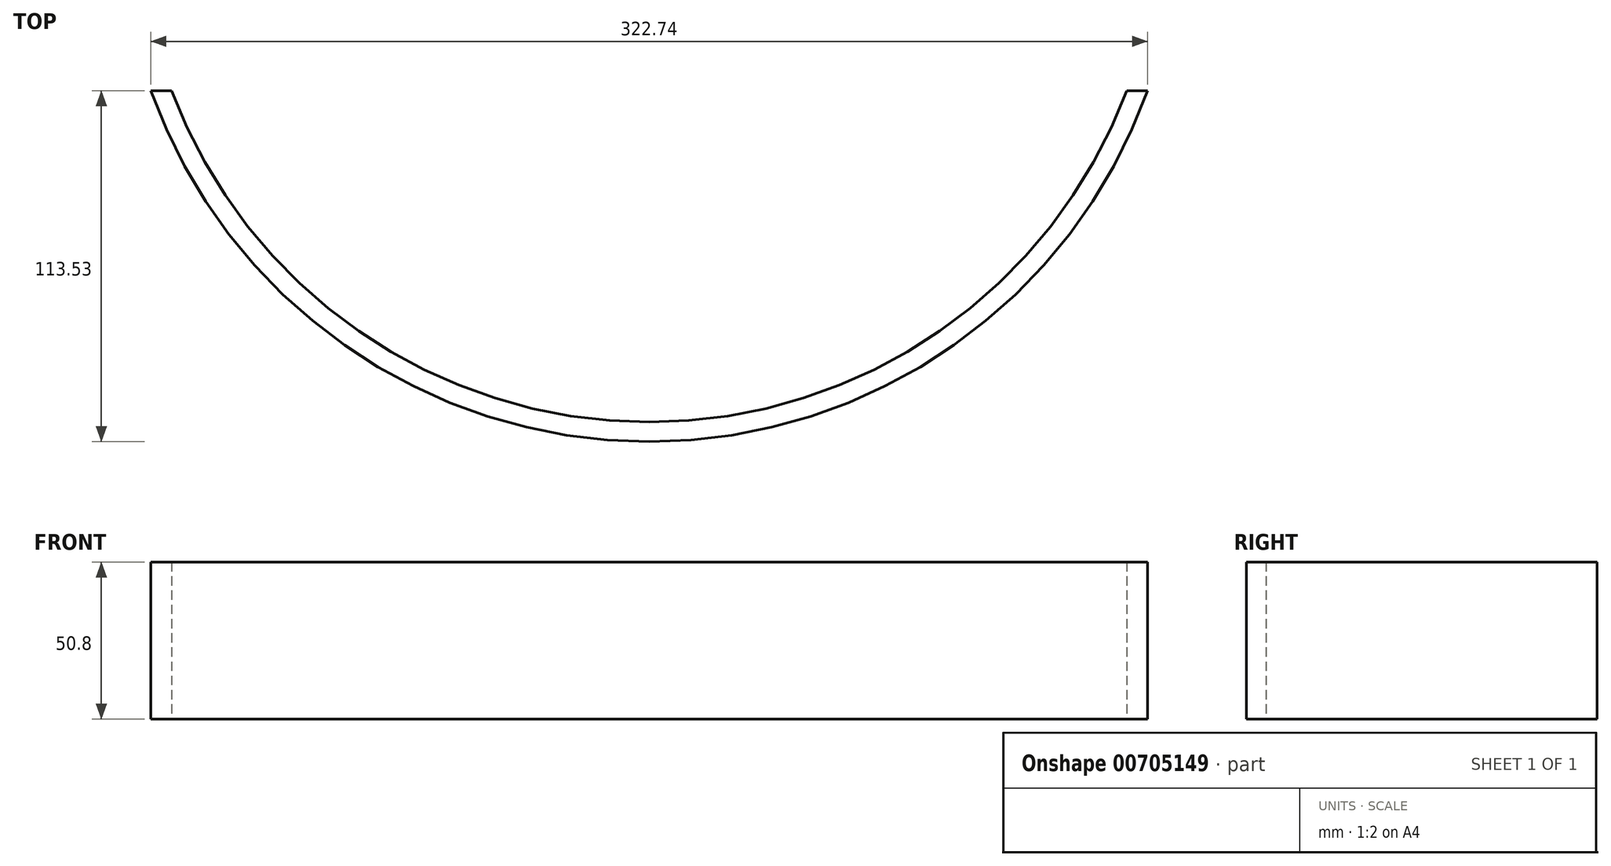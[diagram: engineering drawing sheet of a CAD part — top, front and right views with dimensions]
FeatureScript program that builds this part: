
annotation { "Feature Type Name" : "Feature", "Feature Type Description" : "" }
export const myFeature = defineFeature(function(context is Context, id is Id, definition is map)
    precondition{}
    {
        {
            var Q0;
            Q0=qCreatedBy(makeId("Top.planeOp"),FACE);
            var sketch = newSketch(context, id + "F0", { "sketchPlane" : qUnion([Q0])});
            skArc(sketch, "E0", {"start": v(-154.6, -57.92) * mm, "mid": v(0, -165.1) * mm, "end": v(154.6, -57.92) * mm});
            skArc(sketch, "E1.0", {"start": v(-161.37, -57.92) * mm, "mid": v(0, -171.45) * mm, "end": v(161.37, -57.92) * mm});
            skLineSegment(sketch, "E2.trimOffspring", {"start": v(154.6, -57.92) * mm, "end": v(161.37, -57.92) * mm});
            skLineSegment(sketch, "E3", {"start": v(-161.37, -57.92) * mm, "end": v(-154.6, -57.92) * mm});
            skSolve(sketch);
        }
        {
            var Q0;
            Q0=makeQuery(id+"F0.imprint","IMPRINT",FACE,{"disambiguationData":[TD([[makeQuery(id+"F0.imprint","IMPRINT",EDGE,{"derivedFrom":sQuery(id+"F0.wireOp",EDGE,"E0")}),-1.0]])]});
            extrude(context, id + "F1", {"entities" : qUnion([Q0]), "depth" : 50.8 * mm, "offsetDistance" : 25.4 * mm});
        }
    });
